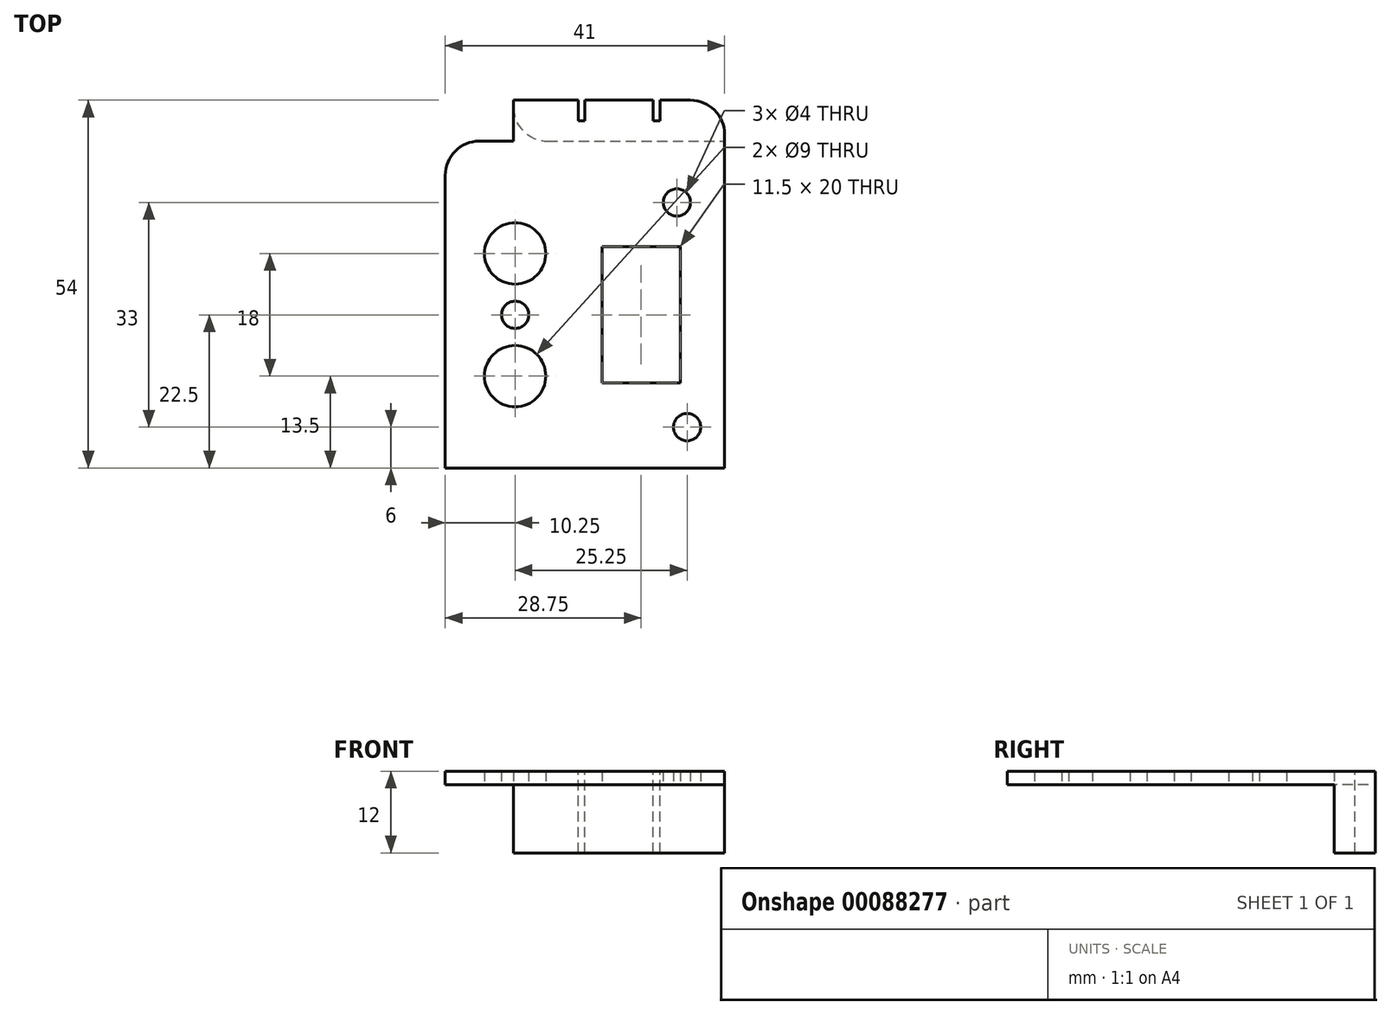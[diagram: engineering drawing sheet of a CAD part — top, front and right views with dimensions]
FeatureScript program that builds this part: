
annotation { "Feature Type Name" : "Feature", "Feature Type Description" : "" }
export const myFeature = defineFeature(function(context is Context, id is Id, definition is map)
    precondition{}
    {
        {
            var Q0;
            Q0=qCreatedBy(makeId("Top.planeOp"),FACE);
            var sketch = newSketch(context, id + "F0", { "sketchPlane" : qUnion([Q0])});
            skLineSegment(sketch, "E0.bottom", {"start": v(0, 0) * mm, "end": v(40, 0) * mm});
            skLineSegment(sketch, "E0.top", {"start": v(0, 48) * mm, "end": v(40, 48) * mm});
            skLineSegment(sketch, "E0.left", {"start": v(0, 0) * mm, "end": v(0, 48) * mm});
            skLineSegment(sketch, "E0.right", {"start": v(40, 0) * mm, "end": v(40, 48) * mm});
            skPoint(sketch, "E1", {"position": v(10.25, 22.5) * mm});
            skCircle(sketch, "E2", {"center": v(10.25, 22.5) * mm, "radius": 2 * mm});
            skPoint(sketch, "E3", {"position": v(23, 12.5) * mm});
            skLineSegment(sketch, "E4.bottom", {"start": v(23, 12.5) * mm, "end": v(34.5, 12.5) * mm});
            skLineSegment(sketch, "E4.top", {"start": v(23, 32.5) * mm, "end": v(34.5, 32.5) * mm});
            skLineSegment(sketch, "E4.left", {"start": v(23, 12.5) * mm, "end": v(23, 32.5) * mm});
            skLineSegment(sketch, "E4.right", {"start": v(34.5, 12.5) * mm, "end": v(34.5, 32.5) * mm});
            skPoint(sketch, "E5", {"position": v(10.25, 31.5) * mm});
            skPoint(sketch, "E6", {"position": v(10.25, 13.5) * mm});
            skCircle(sketch, "E7", {"center": v(10.25, 31.5) * mm, "radius": 4.5 * mm});
            skCircle(sketch, "E8", {"center": v(10.25, 13.5) * mm, "radius": 4.5 * mm});
            skPoint(sketch, "E9", {"position": v(35.5, 6) * mm});
            skPoint(sketch, "E10", {"position": v(34, 39) * mm});
            skCircle(sketch, "E11", {"center": v(34, 39) * mm, "radius": 2 * mm});
            skCircle(sketch, "E12", {"center": v(35.5, 6) * mm, "radius": 2 * mm});
            skSolve(sketch);
        }
        {
            var Q0;
            Q0=qSketchRegion(id+"F0",true);
            extrude(context, id + "F1", {"entities" : qUnion([Q0]), "depth" : 2 * mm});
        }
        {
            var Q0;
            Q0=makeQuery(id+"F1.opExtrude","SWEPT_FACE",FACE,{"disambiguationData":[OSD([sQuery(id+"F0.wireOp",EDGE,"E0.top")])]});
            var sketch = newSketch(context, id + "F2", { "sketchPlane" : qUnion([Q0])});
            skLineSegment(sketch, "E13.bottom", {"start": v(-10, 2) * mm, "end": v(-41, 2) * mm});
            skLineSegment(sketch, "E13.top", {"start": v(-10, -10) * mm, "end": v(-41, -10) * mm});
            skLineSegment(sketch, "E13.left", {"start": v(-10, 2) * mm, "end": v(-10, -10) * mm});
            skLineSegment(sketch, "E13.right", {"start": v(-41, 2) * mm, "end": v(-41, -10) * mm});
            skSolve(sketch);
        }
        {
            var Q0;
            Q0=qSketchRegion(id+"F2",true);
            extrude(context, id + "F3", {"entities" : qUnion([Q0]), "operationType" : NewBodyOperationType.ADD, "depth" : 6 * mm});
        }
        {
            var Q0;
            Q0=makeQuery(id+"F3.opExtrude","CAP_FACE",FACE,{"disambiguationData":[OSD([sQuery(id+"F2.wireOp",EDGE,"E13.bottom"),sQuery(id+"F2.wireOp",EDGE,"E13.top"),sQuery(id+"F2.wireOp",EDGE,"E13.left"),sQuery(id+"F2.wireOp",EDGE,"E13.right")])],"isStart":false});
            var sketch = newSketch(context, id + "F4", { "sketchPlane" : qUnion([Q0])});
            skPoint(sketch, "E14", {"position": v(-25.5, -10) * mm});
            skLineSegment(sketch, "E15.bottom", {"start": v(-20.5, -10) * mm, "end": v(-19.5, -10) * mm});
            skLineSegment(sketch, "E15.top", {"start": v(-20.5, 2) * mm, "end": v(-19.5, 2) * mm});
            skLineSegment(sketch, "E15.left", {"start": v(-20.5, -10) * mm, "end": v(-20.5, 2) * mm});
            skLineSegment(sketch, "E15.right", {"start": v(-19.5, -10) * mm, "end": v(-19.5, 2) * mm});
            skLineSegment(sketch, "E16.bottom", {"start": v(-30.5, -10) * mm, "end": v(-31.5, -10) * mm});
            skLineSegment(sketch, "E16.top", {"start": v(-30.5, 2) * mm, "end": v(-31.5, 2) * mm});
            skLineSegment(sketch, "E16.left", {"start": v(-30.5, -10) * mm, "end": v(-30.5, 2) * mm});
            skLineSegment(sketch, "E16.right", {"start": v(-31.5, -10) * mm, "end": v(-31.5, 2) * mm});
            skSolve(sketch);
        }
        {
            var Q0;
            Q0=qSketchRegion(id+"F4",true);
            extrude(context, id + "F5", {"entities" : qUnion([Q0]), "operationType" : NewBodyOperationType.REMOVE, "oppositeDirection" : true, "depth" : 3 * mm});
        }
        {
            var Q0;
            Q0=makeQuery(id+"F1.opExtrude","SWEPT_FACE",FACE,{"disambiguationData":[OSD([sQuery(id+"F0.wireOp",EDGE,"E0.right")])]});
            extrude(context, id + "F6", {"entities" : qUnion([Q0]), "operationType" : NewBodyOperationType.ADD, "depth" : 1 * mm});
        }
        {
            var Q0;
            {var subQ13=sQuery(id+"F2.wireOp",EDGE,"E13.bottom");var subQ14=sQuery(id+"F2.wireOp",EDGE,"E13.left");Q0=makeQuery(id+"F3.boolean.opBoolean","SPLIT",EDGE,{"disambiguationData":[TD([makeQuery(id+"F3.opExtrude","SWEPT_FACE",FACE,{"disambiguationData":[OSD([subQ13])]})])],"derivedFrom":makeQuery(id+"F3.opExtrude","CAP_EDGE",EDGE,{"disambiguationData":[OSD([subQ14])],"isStart":true})});}
            var Q1;
            Q1=makeQuery(id+"F1.opExtrude","SWEPT_EDGE",EDGE,{"disambiguationData":[OSD([sQuery(id+"F0.wireOp",EDGE,"E0.top"),sQuery(id+"F0.wireOp",EDGE,"E0.left")])]});
            fillet(context, id + "F7", {"entities" : qUnion([Q0, Q1]), "radius" : 5 * mm, "tangentPropagation" : true, "allowEdgeOverflow" : false});
        }
        {
            var Q0;
            Q0=makeQuery(id+"F3.opExtrude","CAP_EDGE",EDGE,{"disambiguationData":[OSD([sQuery(id+"F2.wireOp",EDGE,"E13.right")])],"isStart":false});
            fillet(context, id + "F8", {"entities" : qUnion([Q0]), "radius" : 5 * mm, "tangentPropagation" : true, "allowEdgeOverflow" : false});
        }
    });
